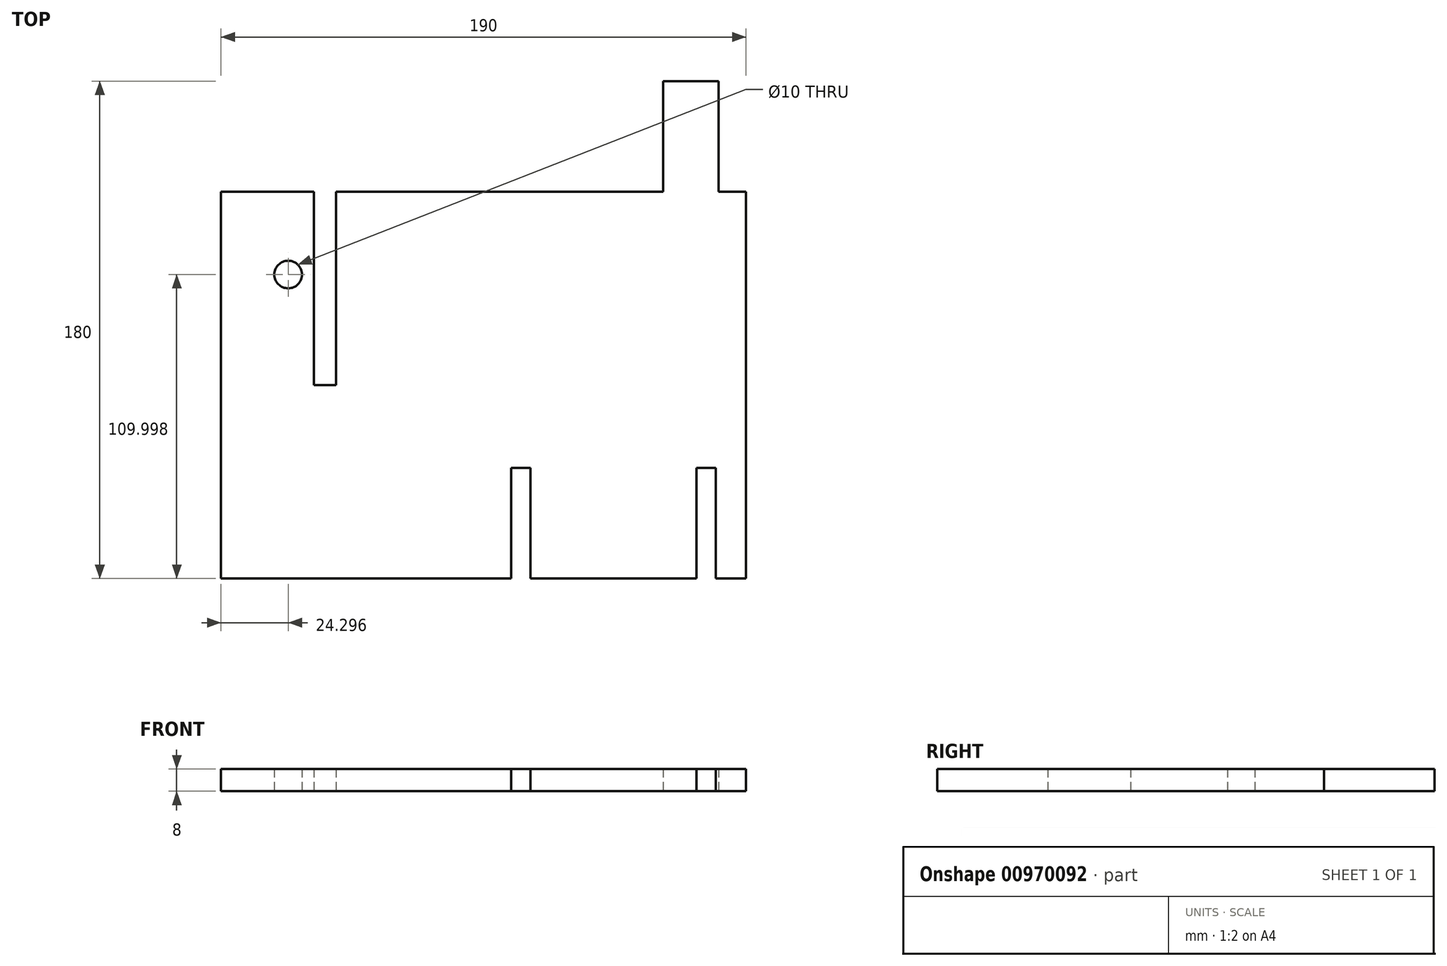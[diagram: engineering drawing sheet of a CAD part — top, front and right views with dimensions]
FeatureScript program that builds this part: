
annotation { "Feature Type Name" : "Feature", "Feature Type Description" : "" }
export const myFeature = defineFeature(function(context is Context, id is Id, definition is map)
    precondition{}
    {
        {
            var Q0;
            Q0=qCreatedBy(makeId("Top.planeOp"),FACE);
            var sketch = newSketch(context, id + "F0", { "sketchPlane" : qUnion([Q0])});
            skLineSegment(sketch, "E0.bottom", {"start": v(-142.5, 106.49) * mm, "end": v(-108.9, 106.49) * mm});
            skLineSegment(sketch, "E0.top", {"start": v(-142.5, -33.51) * mm, "end": v(-37.5, -33.51) * mm});
            skLineSegment(sketch, "E0.left", {"start": v(-142.5, 106.49) * mm, "end": v(-142.5, -33.51) * mm});
            skLineSegment(sketch, "E0.right", {"start": v(47.5, 106.49) * mm, "end": v(47.5, -33.51) * mm});
            skLineSegment(sketch, "E1", {"start": v(36.5, -33.51) * mm, "end": v(36.5, 6.49) * mm});
            skLineSegment(sketch, "E2", {"start": v(36.5, 6.49) * mm, "end": v(29.5, 6.49) * mm});
            skLineSegment(sketch, "E3", {"start": v(29.5, 6.49) * mm, "end": v(29.5, -33.51) * mm});
            skLineSegment(sketch, "E4.trimOffspring", {"start": v(36.5, -33.51) * mm, "end": v(47.5, -33.51) * mm});
            skLineSegment(sketch, "E5", {"start": v(-30.5, -33.51) * mm, "end": v(-30.5, 6.49) * mm});
            skLineSegment(sketch, "E6", {"start": v(-30.5, 6.49) * mm, "end": v(-37.5, 6.49) * mm});
            skLineSegment(sketch, "E7", {"start": v(-37.5, 6.49) * mm, "end": v(-37.5, -33.51) * mm});
            skLineSegment(sketch, "E8.trimOffspring", {"start": v(-30.5, -33.51) * mm, "end": v(29.5, -33.51) * mm});
            skLineSegment(sketch, "E9", {"start": v(-108.9, 106.49) * mm, "end": v(-108.9, 36.49) * mm});
            skLineSegment(sketch, "E10", {"start": v(-108.9, 36.49) * mm, "end": v(-100.9, 36.49) * mm});
            skLineSegment(sketch, "E11", {"start": v(-100.9, 36.49) * mm, "end": v(-100.9, 106.49) * mm});
            skLineSegment(sketch, "E12.trimOffspring", {"start": v(-100.9, 106.49) * mm, "end": v(47.5, 106.49) * mm});
            skLineSegment(sketch, "E13", {"start": v(37.5, 106.49) * mm, "end": v(37.5, 146.49) * mm});
            skLineSegment(sketch, "E14", {"start": v(37.5, 146.49) * mm, "end": v(17.5, 146.49) * mm});
            skLineSegment(sketch, "E15", {"start": v(17.5, 146.49) * mm, "end": v(17.5, 106.49) * mm});
            skCircle(sketch, "E16", {"center": v(-118.2, 76.49) * mm, "radius": 5 * mm});
            skSolve(sketch);
        }
        {
            var Q0;
            Q0 = qSketchRegion(id + "F0", true);
            extrude(context, id + "F1", {"entities" : qUnion([Q0]), "depth" : 8 * mm, "offsetDistance" : 25 * mm});
        }
    });
